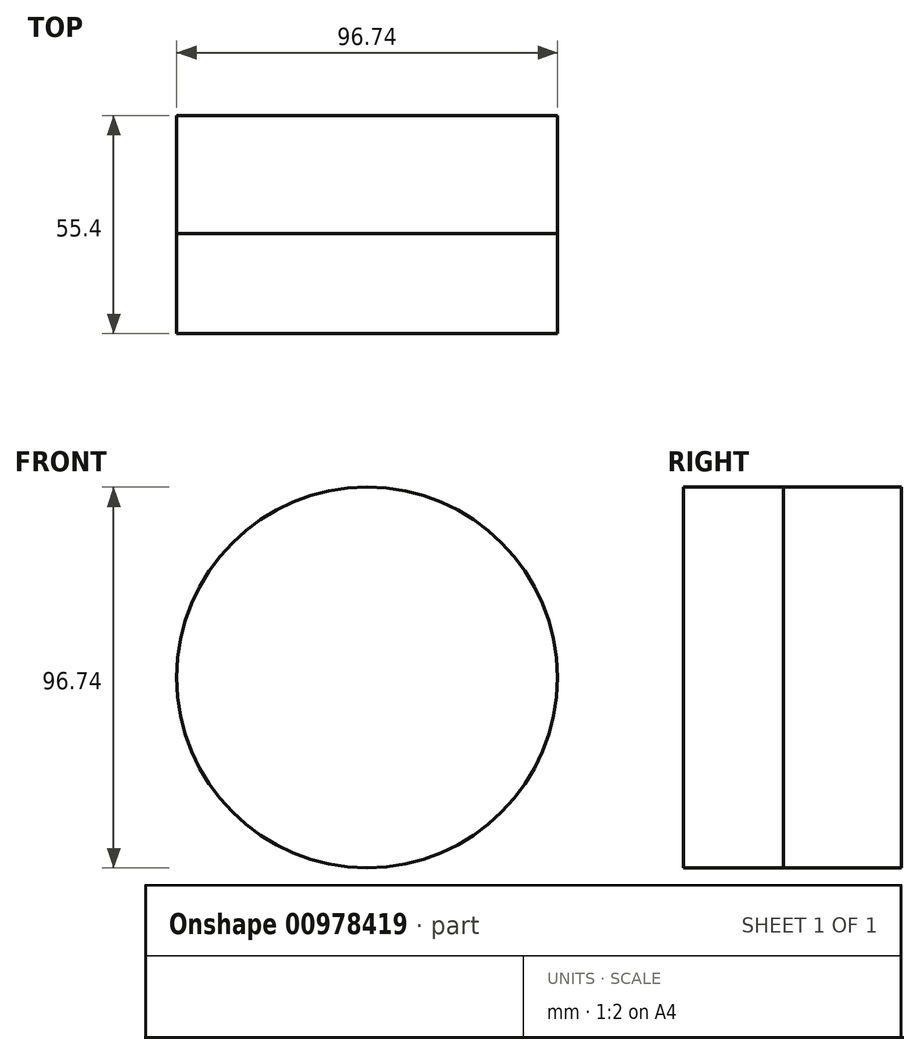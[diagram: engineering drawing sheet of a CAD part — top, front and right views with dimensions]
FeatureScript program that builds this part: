
annotation { "Feature Type Name" : "Feature", "Feature Type Description" : "" }
export const myFeature = defineFeature(function(context is Context, id is Id, definition is map)
    precondition{}
    {
        {
            var Q0;
            Q0=qCreatedBy(makeId("Front.planeOp"),FACE);
            var sketch = newSketch(context, id + "F0", { "sketchPlane" : qUnion([Q0])});
            skCircle(sketch, "E0", {"center": v(0, 0) * mm, "radius": 48.37 * mm});
            skSolve(sketch);
        }
        {
            var Q0;
            Q0=makeQuery(id+"F0.imprint","IMPRINT",FACE,{"disambiguationData":[TD([[makeQuery(id+"F0.imprint","IMPRINT",EDGE,{"derivedFrom":sQuery(id+"F0.wireOp",EDGE,"E0")}),1.0]])]});
            extrude(context, id + "F1", {"entities" : qUnion([Q0]), "depth" : 25.4 * mm, "offsetDistance" : 25.4 * mm});
        }
        {
            var Q0;
            Q0=makeQuery(id+"F1.opExtrude","CAP_FACE",FACE,{"disambiguationData":[OSD([sQuery(id+"F0.wireOp",EDGE,"E0")])],"isStart":true});
            extrude(context, id + "F2", {"entities" : qUnion([Q0]), "depth" : 30 * mm, "offsetDistance" : 25.4 * mm});
        }
    });
